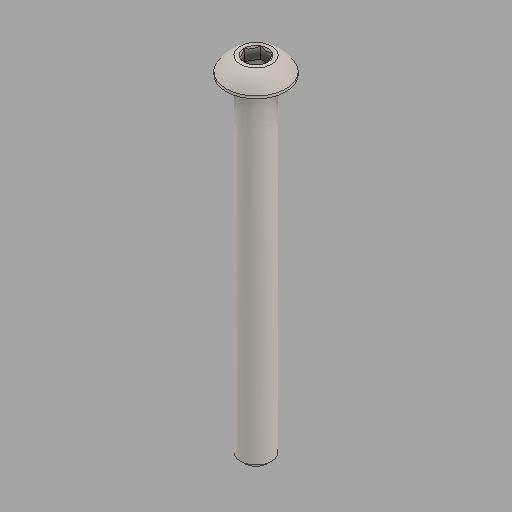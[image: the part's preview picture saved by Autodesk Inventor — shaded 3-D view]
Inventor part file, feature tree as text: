
AUTODESK INVENTOR PART (.ipt)
format: ipt  version: 2024.2 (Build 282272000, 272)  size: 109,056 bytes
history: native  units: in
note: dims shown in document units (in); Inventor stores cm internally (conversion verified against a paired STEP export)
features: fillet x1
ambient origin geometry x8: Origin, YZ Plane, XZ Plane, XY Plane, X Axis, Y Axis, Z Axis, Center Point
bodies: Solid1 (feature_tree)
feature tree (1):
  fillet  "Fillet1"  [1 undecoded]
note: 1 required parameter value undecoded (feature->parameter linkage not recoverable at this tier; creation-order binding heuristic only, values carry confidence <= 0.55)
